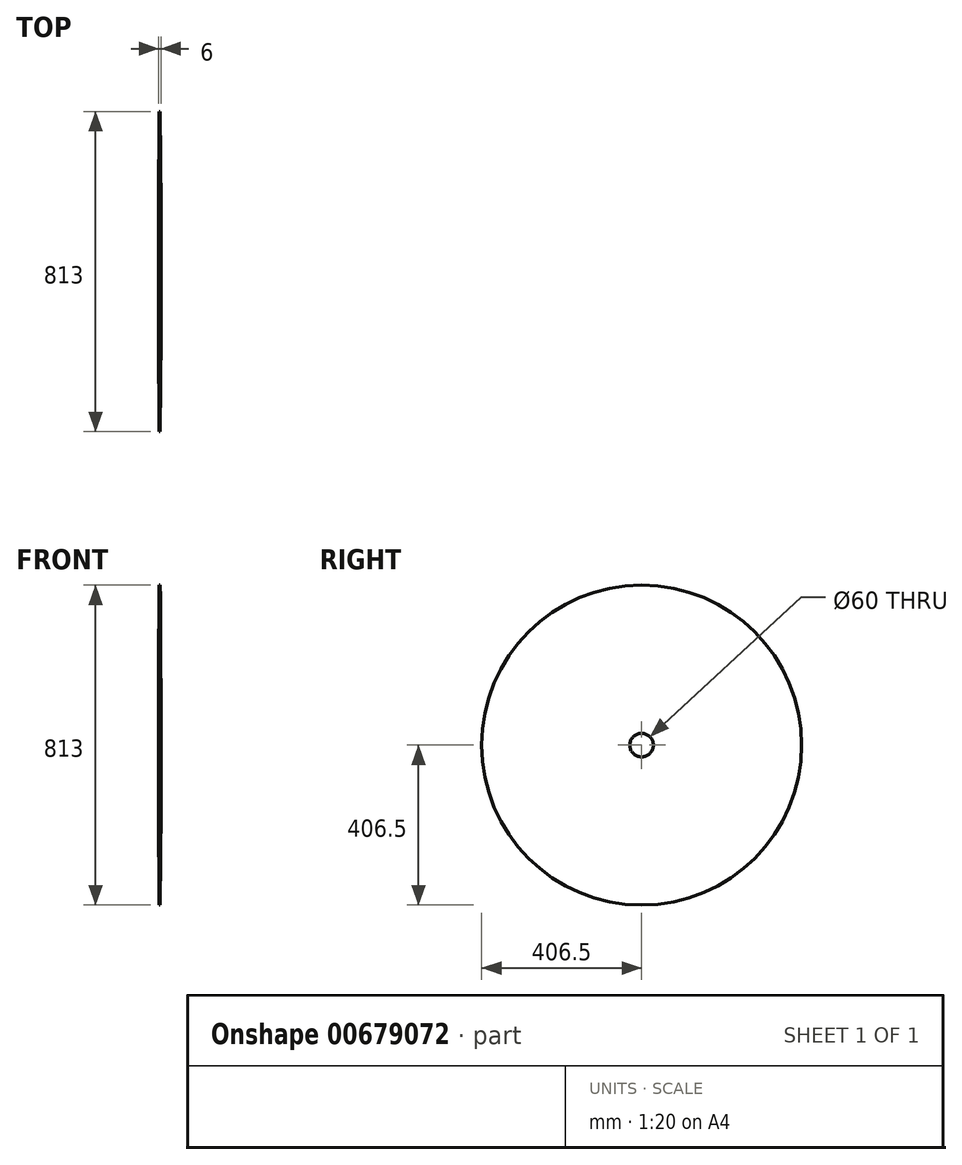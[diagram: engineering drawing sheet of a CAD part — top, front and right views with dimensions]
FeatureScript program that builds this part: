
annotation { "Feature Type Name" : "Feature", "Feature Type Description" : "" }
export const myFeature = defineFeature(function(context is Context, id is Id, definition is map)
    precondition{}
    {
        {
            var Q0;
            Q0=qCreatedBy(makeId("Front.planeOp"),FACE);
            var sketch = newSketch(context, id + "F0", { "sketchPlane" : qUnion([Q0])});
            skLineSegment(sketch, "E0", {"start": v(0, 0) * mm, "end": v(60, 0) * mm, "construction": true});
            skLineSegment(sketch, "E1", {"start": v(30, 30) * mm, "end": v(36, 30) * mm});
            skLineSegment(sketch, "E2", {"start": v(36, 30) * mm, "end": v(36, 165) * mm});
            skLineSegment(sketch, "E3", {"start": v(36, 165) * mm, "end": v(34.5, 406.5) * mm});
            skLineSegment(sketch, "E4", {"start": v(34.5, 406.5) * mm, "end": v(31.5, 406.5) * mm});
            skLineSegment(sketch, "E5", {"start": v(31.5, 406.5) * mm, "end": v(30, 165) * mm});
            skLineSegment(sketch, "E6", {"start": v(30, 165) * mm, "end": v(30, 30) * mm});
            skSolve(sketch);
        }
        {
            var Q0;
            Q0=makeQuery(id+"F0.imprint","IMPRINT",FACE,{"disambiguationData":[TD([[makeQuery(id+"F0.imprint","IMPRINT",EDGE,{"derivedFrom":sQuery(id+"F0.wireOp",EDGE,"E1")}),1.0]])]});
            var Q1;
            Q1=sQuery(id+"F0.wireOp",EDGE,"E0");
            revolve(context, id + "F1", {"entities" : qUnion([Q0]), "axis" : qUnion([Q1]), "revolveType" : RevolveType.FULL});
        }
    });
